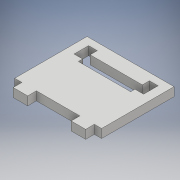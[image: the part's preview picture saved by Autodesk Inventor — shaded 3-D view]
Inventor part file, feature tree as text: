
AUTODESK INVENTOR PART (.ipt)
format: ipt  version: 2017 (Build 210142000, 142)  size: 127,488 bytes
history: native  units: mm
features: extrude x1, sketch x1
ambient origin geometry x8: Origin, YZ Plane, XZ Plane, XY Plane, X Axis, Y Axis, Z Axis, Center Point
bodies: Solide1 (feature_tree)
feature tree (2):
  extrude  "Extrusion1"  Depth=50.0mm
  sketch  "Esquisse1"
